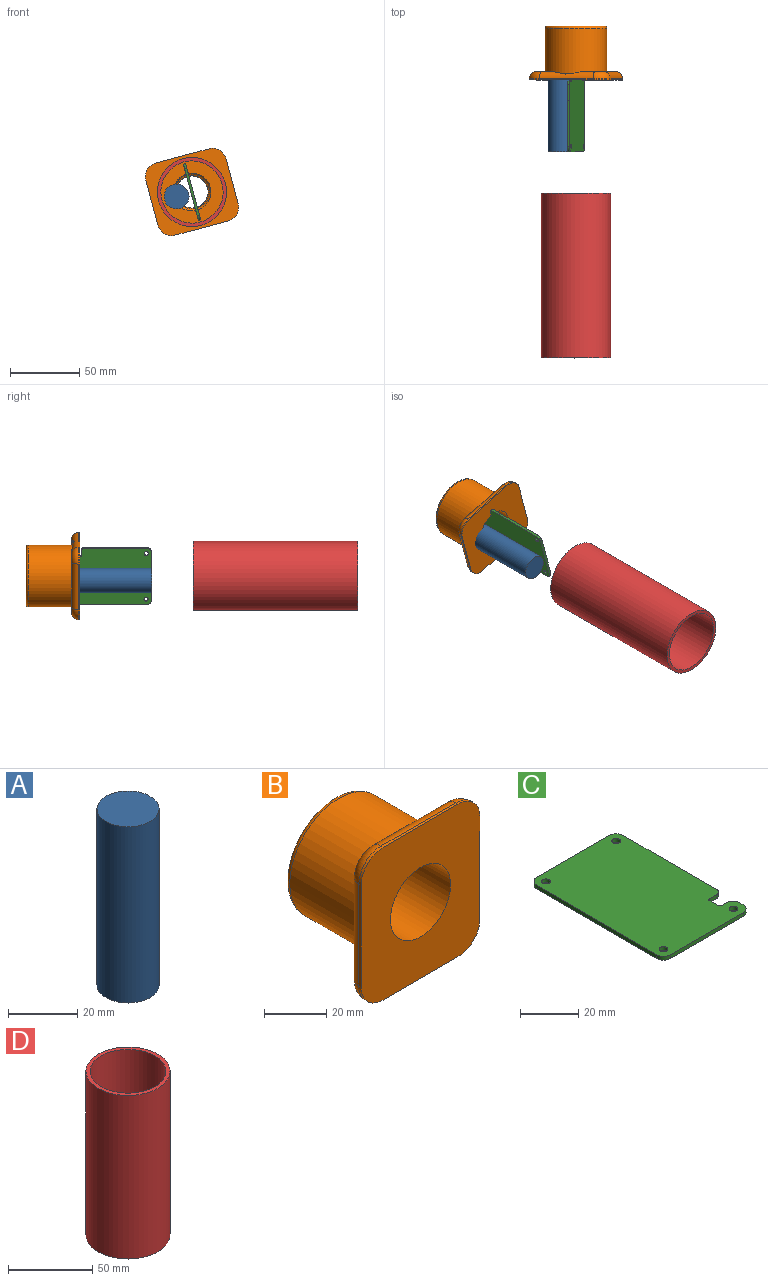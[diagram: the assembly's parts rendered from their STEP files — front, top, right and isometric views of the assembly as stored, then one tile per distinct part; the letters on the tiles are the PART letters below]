
ASSEMBLY  parts=4 mates=1
PART A: 3 faces, bbox 18x18x62.5 mm
  f0: cylinder r=9mm len=62.5mm, axis (0,0,-1), area 3534.3mm2, adj f1,f2
  f1: plane 18x18mm, normal (0,0,1), area 254.5mm2, adj f0
  f2: plane 18x18mm, normal (0,0,-1), area 254.5mm2, adj f0
PART B: 41 faces, bbox 55.6x42.2x61.6 mm
  f0: plane 16.49x11.91mm, normal (0,1,0), area 64mm2, adj f27,f29,f31,f39
  f1: plane 16.49x11.91mm, normal (0,1,0), area 64mm2, adj f28,f30,f31,f38
  f2: plane 16.49x11.91mm, normal (0,1,0), area 64mm2, adj f24,f25,f27,f35
  f3: cylinder r=22.35mm len=44.7mm, axis (0,1,0), area 4774.6mm2, adj f23,f32
  f4: cylinder r=11.65mm len=23.3mm, axis (0,-1,0), area 1.6mm2, adj f6,f8,f9,f10
  f5: plane 40.7x40.7mm, normal (0,1,0), area 715.7mm2, adj f6,f32
  f6: cone r=11.65mm half-angle=45deg, axis (0,1,0), area 144.3mm2, adj f4,f5,f9,f10
  f7: cone r=11.65mm half-angle=45deg, axis (0,-1,0), area 131.3mm2, adj f8,f9,f10,f11
  f8: cone r=11.65mm half-angle=45deg, axis (0,-1,0), area 13mm2, adj f4,f7,f9,f10
  f9: bspline ~30.37x26.3mm, area 870.5mm2, adj f4,f6,f7,f8,f10
  f10: bspline ~30.37x26.3mm, area 867.1mm2, adj f4,f6,f7,f8,f9
  f11: cylinder r=13.65mm len=27.3mm, axis (0,1,0), area 2144.1mm2, adj f7,f12
  f12: plane 60x54mm, normal (0,-1,0), area 2568.8mm2, adj f11,f14,f15,f16,f17,f18,f19,f20
  f13: plane 16.49x11.91mm, normal (0,1,0), area 64mm2, adj f24,f26,f28,f34
  f14: plane 40x1mm, normal (1,0,0), area 40mm2, adj f12,f15,f21,f24
  f15: cylinder r=10mm len=10mm, axis (0,-1,0), area 15.7mm2, adj f12,f14,f16,f25
  f16: plane 34x1mm, normal (0,0,1), area 34mm2, adj f12,f15,f17,f27
  f17: cylinder r=10mm len=10mm, axis (0,-1,0), area 15.7mm2, adj f12,f16,f18,f29
  f18: plane 40x1mm, normal (-1,0,0), area 40mm2, adj f12,f17,f19,f31
  f19: cylinder r=10mm len=10mm, axis (0,-1,0), area 15.7mm2, adj f12,f18,f20,f30
  f20: plane 34x1mm, normal (0,0,-1), area 34mm2, adj f12,f19,f21,f28
  f21: cylinder r=10mm len=10mm, axis (0,-1,0), area 15.7mm2, adj f12,f14,f20,f26
  f22: cylinder r=25.3mm len=50.6mm, axis (0,1,0), area 383.2mm2, adj f23,f33,f34,f35,f36,f37,f38,f39
  f23: plane 50.6x50.6mm, normal (0,1,0), area 441.6mm2, adj f3,f22
  f24: cylinder r=5mm len=40mm, axis (0,0,-1), area 240.3mm2, adj f2,f13,f14,f25,f26,f33
  f25: torus R=5mm, axis (0,-1,0), area 101mm2, adj f2,f15,f24,f27
  f26: torus R=5mm, axis (0,-1,0), area 101mm2, adj f13,f21,f24,f28
  f27: cylinder r=5mm len=34mm, axis (1,0,0), area 262.3mm2, adj f0,f2,f16,f25,f29,f37
  f28: cylinder r=5mm len=34mm, axis (-1,0,0), area 262.3mm2, adj f1,f13,f20,f26,f30,f36
  f29: torus R=5mm, axis (0,-1,0), area 101mm2, adj f0,f17,f27,f31
  f30: torus R=5mm, axis (0,-1,0), area 101mm2, adj f1,f19,f28,f31
  f31: cylinder r=5mm len=40mm, axis (0,0,1), area 240.3mm2, adj f0,f1,f18,f29,f30,f40
  f32: torus R=20.35mm, axis (0,-1,0), area 426.8mm2, adj f3,f5
  f33: bspline ~27.97x4.84mm, area 17.4mm2, adj f22,f24,f34,f35
  f34: torus R=25.6mm, axis (0,-1,0), area 9.8mm2, adj f13,f22,f33,f36
  f35: torus R=25.6mm, axis (0,-1,0), area 9.8mm2, adj f2,f22,f33,f37
  f36: bspline ~15.09x1.55mm, area 5.5mm2, adj f22,f28,f34,f38
  f37: bspline ~15.09x1.55mm, area 5.5mm2, adj f22,f27,f35,f39
  f38: torus R=25.6mm, axis (0,-1,0), area 9.8mm2, adj f1,f22,f36,f40
  f39: torus R=25.6mm, axis (0,-1,0), area 9.8mm2, adj f0,f22,f37,f40
  f40: bspline ~27.97x4.84mm, area 17.4mm2, adj f22,f31,f38,f39
PART C: 23 faces, bbox 42x65x1.6 mm
  f0: plane 11.8x1.6mm, normal (1,0,0), area 18.9mm2, adj f1,f20,f21,f22
  f1: plane 33.31x1.6mm, normal (1,0,0), area 53.3mm2, adj f0,f2,f21,f22
  f2: cylinder r=3.74mm len=3.75mm, axis (0,0,-1), area 9.4mm2, adj f1,f3,f21,f22
  f3: plane 34.63x1.6mm, normal (0,1,0), area 55.4mm2, adj f2,f4,f21,f22
  f4: cylinder r=3.62mm len=3.62mm, axis (0,0,-1), area 9.1mm2, adj f3,f5,f21,f22
  f5: plane 58.21x1.6mm, normal (-1,0,0), area 93.1mm2, adj f4,f6,f21,f22
  f6: cylinder r=3.17mm len=3.18mm, axis (0,0,-1), area 8mm2, adj f5,f7,f21,f22
  f7: plane 35.56x1.6mm, normal (0,-1,0), area 56.9mm2, adj f6,f8,f21,f22
  f8: cylinder r=3.17mm len=3.18mm, axis (0,0,-1), area 8mm2, adj f7,f9,f21,f22
  f9: plane 1.91x1.6mm, normal (1,0,0), area 3mm2, adj f8,f10,f21,f22
  f10: cylinder r=3.17mm len=3.18mm, axis (0,0,-1), area 8mm2, adj f9,f11,f21,f22
  f11: plane 2.54x1.6mm, normal (0,1,0), area 4.1mm2, adj f10,f12,f21,f22
  f12: cylinder r=0.64mm len=1.6mm, axis (0,0,-1), area 1.6mm2, adj f11,f13,f21,f22
  f13: plane 4.45x1.6mm, normal (1,0,0), area 7.1mm2, adj f12,f14,f21,f22
  f14: cylinder r=0.64mm len=1.6mm, axis (0,0,-1), area 1.6mm2, adj f13,f15,f21,f22
  f15: plane 3.55x1.6mm, normal (0,-1,0), area 5.7mm2, adj f14,f20,f21,f22
  f16: cylinder r=1.5mm len=3mm, axis (0,0,-1), area 15.1mm2, adj f21,f22
  f17: cylinder r=1.5mm len=3mm, axis (0,0,-1), area 15.1mm2, adj f21,f22
  f18: cylinder r=1.5mm len=3mm, axis (0,0,-1), area 15.1mm2, adj f21,f22
  f19: cylinder r=1.5mm len=3mm, axis (0,0,-1), area 15.1mm2, adj f21,f22
  f20: cylinder r=2.17mm len=2.17mm, axis (0,0,-1), area 5.4mm2, adj f0,f15,f21,f22
  f21: plane 65x41.99mm, normal (0,0,1), area 2648.1mm2, adj f0,f1,f2,f3,f4,f5,f6,f7
  f22: plane 65x41.99mm, normal (0,0,-1), area 2648.1mm2, adj f0,f1,f2,f3,f4,f5,f6,f7
PART D: 4 faces, bbox 50x50x119 mm
  f0: cylinder r=22.5mm len=119mm, axis (0,0,-1), area 16823.2mm2, adj f2,f3
  f1: cylinder r=25mm len=119mm, axis (0,0,-1), area 18692.5mm2, adj f2,f3
  f2: plane 50x50mm, normal (0,0,1), area 373.1mm2, adj f0,f1
  f3: plane 50x50mm, normal (0,0,-1), area 373.1mm2, adj f0,f1
PLACE A rot(axis=(1,0,0),90deg) t=(23.56,36.69,11.2)mm
PLACE B rot(axis=(0,1,0),75deg) t=(34.72,64.98,14.47)mm
PLACE C rot(axis=(-0.61,0,-0.79),179.9deg) t=(33.93,6.55,14.34)mm
PLACE D rot(axis=(-0.48,-0.62,-0.62),129deg) t=(34.72,-175.03,14.47)mm
MATE cylindrical D.f0 <-> B.f3  axis (0,-1,0) through (34.72,-56.03,14.47)mm
